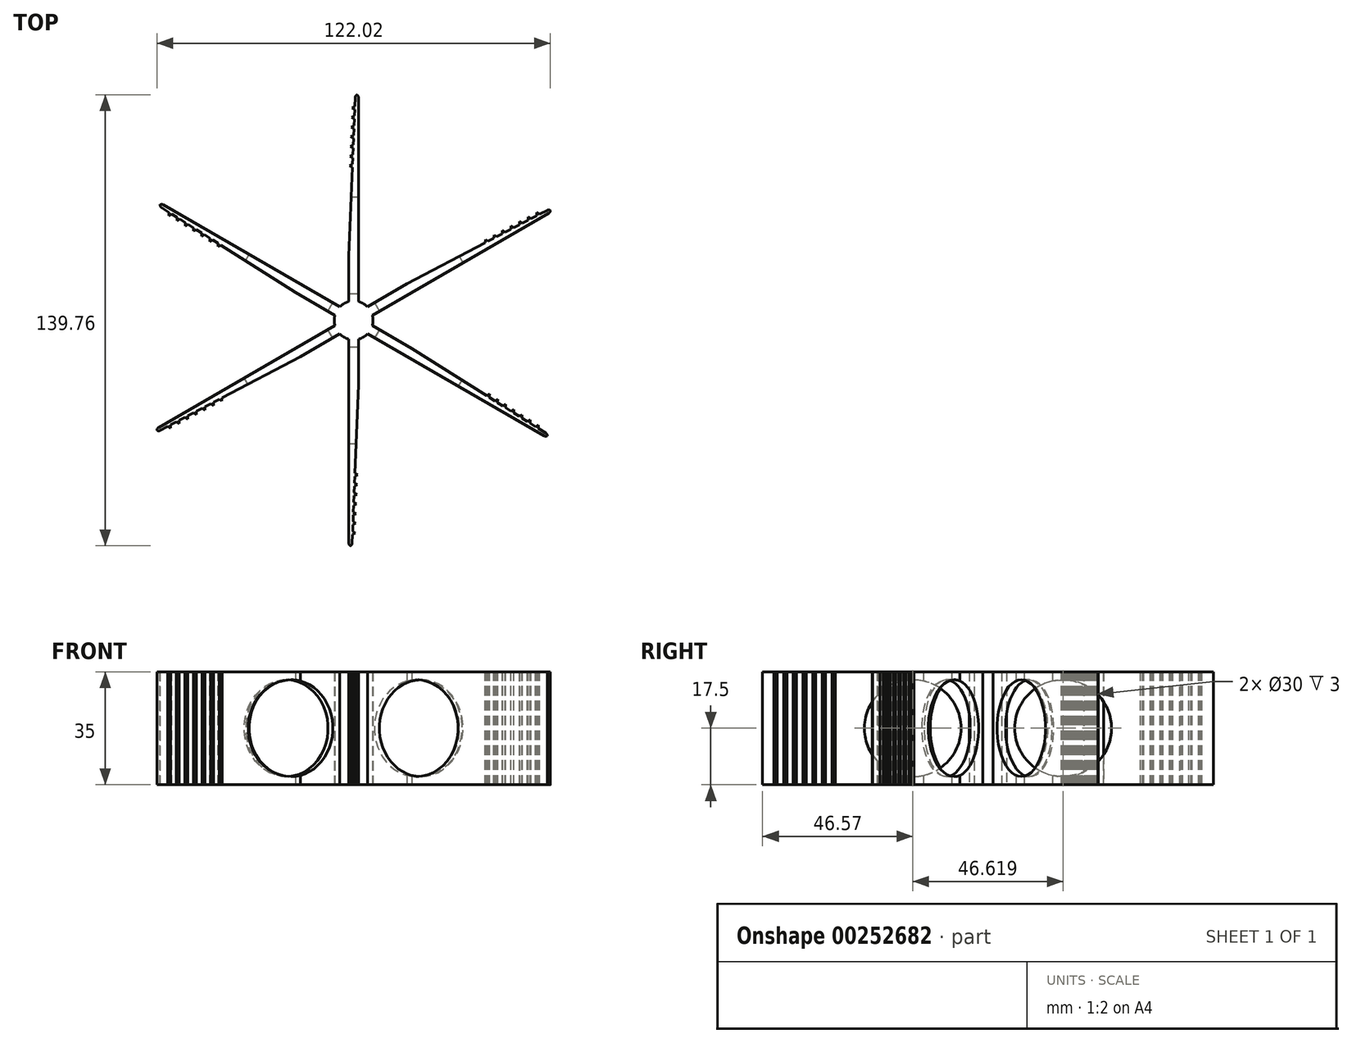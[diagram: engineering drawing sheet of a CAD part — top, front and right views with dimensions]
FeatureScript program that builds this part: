
annotation { "Feature Type Name" : "Feature", "Feature Type Description" : "" }
export const myFeature = defineFeature(function(context is Context, id is Id, definition is map)
    precondition{}
    {
        {
            var Q0;
            Q0=qCreatedBy(makeId("Top.planeOp"),FACE);
            var sketch = newSketch(context, id + "F0", { "sketchPlane" : qUnion([Q0])});
            skLineSegment(sketch, "E0.bottom", {"start": v(-1.5, 70) * mm, "end": v(1.5, 70) * mm});
            skLineSegment(sketch, "E0.top", {"start": v(-1.5, 0) * mm, "end": v(1.5, 0) * mm});
            skLineSegment(sketch, "E0.left", {"start": v(-1.5, 70) * mm, "end": v(-1.5, 0) * mm});
            skLineSegment(sketch, "E0.right", {"start": v(1.5, 70) * mm, "end": v(1.5, 0) * mm});
            skCircle(sketch, "E1", {"center": v(0, 0) * mm, "radius": 6 * mm});
            skSolve(sketch);
        }
        {
            var Q0;
            Q0 = qSketchRegion(id + "F0", true);
            extrude(context, id + "F1", {"entities" : qUnion([Q0]), "depth" : 35 * mm});
        }
        {
            var Q0;
            Q0=makeQuery(id+"F1.opExtrude","SWEPT_EDGE",EDGE,{"disambiguationData":[OSD([sQuery(id+"F0.wireOp",EDGE,"E0.bottom"),sQuery(id+"F0.wireOp",EDGE,"E0.left")])]});
            chamfer(context, id + "F2", {"entities" : qUnion([Q0]), "chamferType" : ChamferType.TWO_OFFSETS, "width1" : 2 * mm, "oppositeDirection" : true, "width2" : 50 * mm, "tangentPropagation" : true});
        }
        {
            var Q0;
            Q0=makeQuery(id+"F1.opExtrude","SWEPT_EDGE",EDGE,{"disambiguationData":[OSD([sQuery(id+"F0.wireOp",EDGE,"E0.bottom"),sQuery(id+"F0.wireOp",EDGE,"E0.right")])]});
            var Q1;
            {var subQ0=sQuery(id+"F0.wireOp",EDGE,"E0.bottom");Q1=makeQuery(id+"F2.opChamfer","BLEND_EDGE",EDGE,{"blendedFrom":[makeQuery(id+"F1.opExtrude","SWEPT_EDGE",EDGE,{"disambiguationData":[OSD([subQ0,sQuery(id+"F0.wireOp",EDGE,"E0.left")])]}),makeQuery(id+"F1.opExtrude","SWEPT_FACE",FACE,{"disambiguationData":[OSD([subQ0])]})],"blendedInto":[makeQuery(id+"F1.opExtrude","SWEPT_FACE",FACE,{"disambiguationData":[OSD([subQ0])]})]});}
            fillet(context, id + "F3", {"entities" : qUnion([Q0, Q1]), "radius" : 1 * mm, "tangentPropagation" : true, "allowEdgeOverflow" : false});
        }
        {
            var Q0;
            Q0=makeQuery(id+"F1.opExtrude","SWEPT_FACE",FACE,{"disambiguationData":[OSD([sQuery(id+"F0.wireOp",EDGE,"E0.right")])]});
            var sketch = newSketch(context, id + "F4", { "sketchPlane" : qUnion([Q0])});
            skCircle(sketch, "E2", {"center": v(23.3, 17.5) * mm, "radius": 15 * mm});
            skSolve(sketch);
        }
        {
            var Q0;
            Q0=makeQuery(id+"F4.imprint","IMPRINT",FACE,{"disambiguationData":[TD([[makeQuery(id+"F4.imprint","IMPRINT",EDGE,{"derivedFrom":sQuery(id+"F4.wireOp",EDGE,"E2")}),1.0]])]});
            extrude(context, id + "F5", {"entities" : qUnion([Q0]), "operationType" : NewBodyOperationType.REMOVE, "endBound" : BoundingType.UP_TO_NEXT, "oppositeDirection" : true, "depth" : 25 * mm});
        }
        {
            var Q0;
            Q0=makeQuery(id+"F1.opExtrude","CAP_FACE",FACE,{"disambiguationData":[OSD([sQuery(id+"F0.wireOp",EDGE,"E0.bottom"),sQuery(id+"F0.wireOp",EDGE,"E0.left"),sQuery(id+"F0.wireOp",EDGE,"E0.right"),sQuery(id+"F0.wireOp",EDGE,"E1")])],"isStart":false});
            var sketch = newSketch(context, id + "F6", { "sketchPlane" : qUnion([Q0])});
            skLineSegment(sketch, "E3", {"start": v(0.35, 66.34) * mm, "end": v(-0.53, 65.87) * mm});
            skLineSegment(sketch, "E4", {"start": v(-0.53, 65.87) * mm, "end": v(0.31, 65.34) * mm});
            skLineSegment(sketch, "E5.1.0.0", {"start": v(0.23, 63.34) * mm, "end": v(-0.65, 62.88) * mm});
            skLineSegment(sketch, "E5.1.0.1", {"start": v(-0.65, 62.88) * mm, "end": v(0.2, 62.34) * mm});
            skLineSegment(sketch, "E5.2.0.0", {"start": v(0.11, 60.35) * mm, "end": v(-0.77, 59.88) * mm});
            skLineSegment(sketch, "E5.2.0.1", {"start": v(-0.77, 59.88) * mm, "end": v(0.07, 59.35) * mm});
            skLineSegment(sketch, "E5.3.0.0", {"start": v(0, 57.35) * mm, "end": v(-0.9, 56.88) * mm});
            skLineSegment(sketch, "E5.3.0.1", {"start": v(-0.9, 56.88) * mm, "end": v(-0.05, 56.35) * mm});
            skLineSegment(sketch, "E5.4.0.0", {"start": v(-0.13, 54.35) * mm, "end": v(-1.01, 53.88) * mm});
            skLineSegment(sketch, "E5.4.0.1", {"start": v(-1.01, 53.88) * mm, "end": v(-0.17, 53.35) * mm});
            skLineSegment(sketch, "E5.5.0.0", {"start": v(-0.25, 51.35) * mm, "end": v(-1.13, 50.89) * mm});
            skLineSegment(sketch, "E5.5.0.1", {"start": v(-1.13, 50.89) * mm, "end": v(-0.29, 50.35) * mm});
            skLineSegment(sketch, "E5.6.0.0", {"start": v(-0.37, 48.35) * mm, "end": v(-1.25, 47.89) * mm});
            skLineSegment(sketch, "E5.6.0.1", {"start": v(-1.25, 47.89) * mm, "end": v(-0.4, 47.35) * mm});
            skLineSegment(sketch, "E5.direction1", {"start": v(-0.53, 65.87) * mm, "end": v(-0.65, 62.88) * mm, "construction": true});
            skSolve(sketch);
        }
        {
            var Q0;
            {var subQ0=sQuery(id+"F6.wireOp",EDGE,"E5.6.0.1");var subQ1=sQuery(id+"F6.wireOp",EDGE,"E5.6.0.0");var subQ2=makeQuery(id+"F6.imprint","INTERSECT",VERTEX,{"derivedFrom":[subQ1,subQ0]});Q0=makeQuery(id+"F6.imprint","IMPRINT",FACE,{"disambiguationData":[TD([[makeQuery(id+"F6.imprint","IMPRINT",EDGE,{"disambiguationData":[TD([[subQ2,1.0]])],"derivedFrom":subQ1}),1.0]])]});}
            var Q1;
            {var subQ0=sQuery(id+"F6.wireOp",EDGE,"E5.5.0.1");var subQ1=sQuery(id+"F6.wireOp",EDGE,"E5.5.0.0");var subQ2=makeQuery(id+"F6.imprint","INTERSECT",VERTEX,{"derivedFrom":[subQ1,subQ0]});Q1=makeQuery(id+"F6.imprint","IMPRINT",FACE,{"disambiguationData":[TD([[makeQuery(id+"F6.imprint","IMPRINT",EDGE,{"disambiguationData":[TD([[subQ2,1.0]])],"derivedFrom":subQ1}),1.0]])]});}
            var Q2;
            {var subQ0=sQuery(id+"F6.wireOp",EDGE,"E5.4.0.1");var subQ1=sQuery(id+"F6.wireOp",EDGE,"E5.4.0.0");var subQ2=makeQuery(id+"F6.imprint","INTERSECT",VERTEX,{"derivedFrom":[subQ1,subQ0]});Q2=makeQuery(id+"F6.imprint","IMPRINT",FACE,{"disambiguationData":[TD([[makeQuery(id+"F6.imprint","IMPRINT",EDGE,{"disambiguationData":[TD([[subQ2,1.0]])],"derivedFrom":subQ1}),1.0]])]});}
            var Q3;
            {var subQ0=sQuery(id+"F6.wireOp",EDGE,"E5.3.0.1");var subQ1=sQuery(id+"F6.wireOp",EDGE,"E5.3.0.0");var subQ2=makeQuery(id+"F6.imprint","INTERSECT",VERTEX,{"derivedFrom":[subQ1,subQ0]});Q3=makeQuery(id+"F6.imprint","IMPRINT",FACE,{"disambiguationData":[TD([[makeQuery(id+"F6.imprint","IMPRINT",EDGE,{"disambiguationData":[TD([[subQ2,1.0]])],"derivedFrom":subQ1}),1.0]])]});}
            var Q4;
            {var subQ0=sQuery(id+"F6.wireOp",EDGE,"E5.2.0.1");var subQ1=sQuery(id+"F6.wireOp",EDGE,"E5.2.0.0");var subQ2=makeQuery(id+"F6.imprint","INTERSECT",VERTEX,{"derivedFrom":[subQ1,subQ0]});Q4=makeQuery(id+"F6.imprint","IMPRINT",FACE,{"disambiguationData":[TD([[makeQuery(id+"F6.imprint","IMPRINT",EDGE,{"disambiguationData":[TD([[subQ2,1.0]])],"derivedFrom":subQ1}),1.0]])]});}
            var Q5;
            {var subQ0=sQuery(id+"F6.wireOp",EDGE,"E5.1.0.0");Q5=makeQuery(id+"F6.imprint","IMPRINT",FACE,{"disambiguationData":[TD([[makeQuery(id+"F6.imprint","IMPRINT",EDGE,{"derivedFrom":subQ0}),1.0]])]});}
            var Q6;
            {var subQ0=sQuery(id+"F6.wireOp",EDGE,"E3");Q6=makeQuery(id+"F6.imprint","IMPRINT",FACE,{"disambiguationData":[TD([[makeQuery(id+"F6.imprint","IMPRINT",EDGE,{"derivedFrom":subQ0}),1.0]])]});}
            extrude(context, id + "F7", {"entities" : qUnion([Q0, Q1, Q2, Q3, Q4, Q5, Q6]), "operationType" : NewBodyOperationType.ADD, "oppositeDirection" : true, "depth" : 35 * mm});
        }
        {
            var Q0;
            Q0=makeQuery(id+"F1.opExtrude","SWEPT_BODY",BODY,{"disambiguationData":[OSD([sQuery(id+"F0.wireOp",EDGE,"E0.bottom"),sQuery(id+"F0.wireOp",EDGE,"E0.left"),sQuery(id+"F0.wireOp",EDGE,"E0.right"),sQuery(id+"F0.wireOp",EDGE,"E1")])]});
            var Q1;
            Q1=makeQuery(id+"F1.opExtrude","SWEPT_FACE",FACE,{"disambiguationData":[OSD([sQuery(id+"F0.wireOp",EDGE,"E1")])]});
            circularPattern(context, id + "F8", {"operationType" : NewBodyOperationType.ADD, "entities" : qUnion([Q0]), "axis" : qUnion([Q1]), "angle" : 360 * degree, "instanceCount" : 6, "equalSpace" : true});
        }
    });
